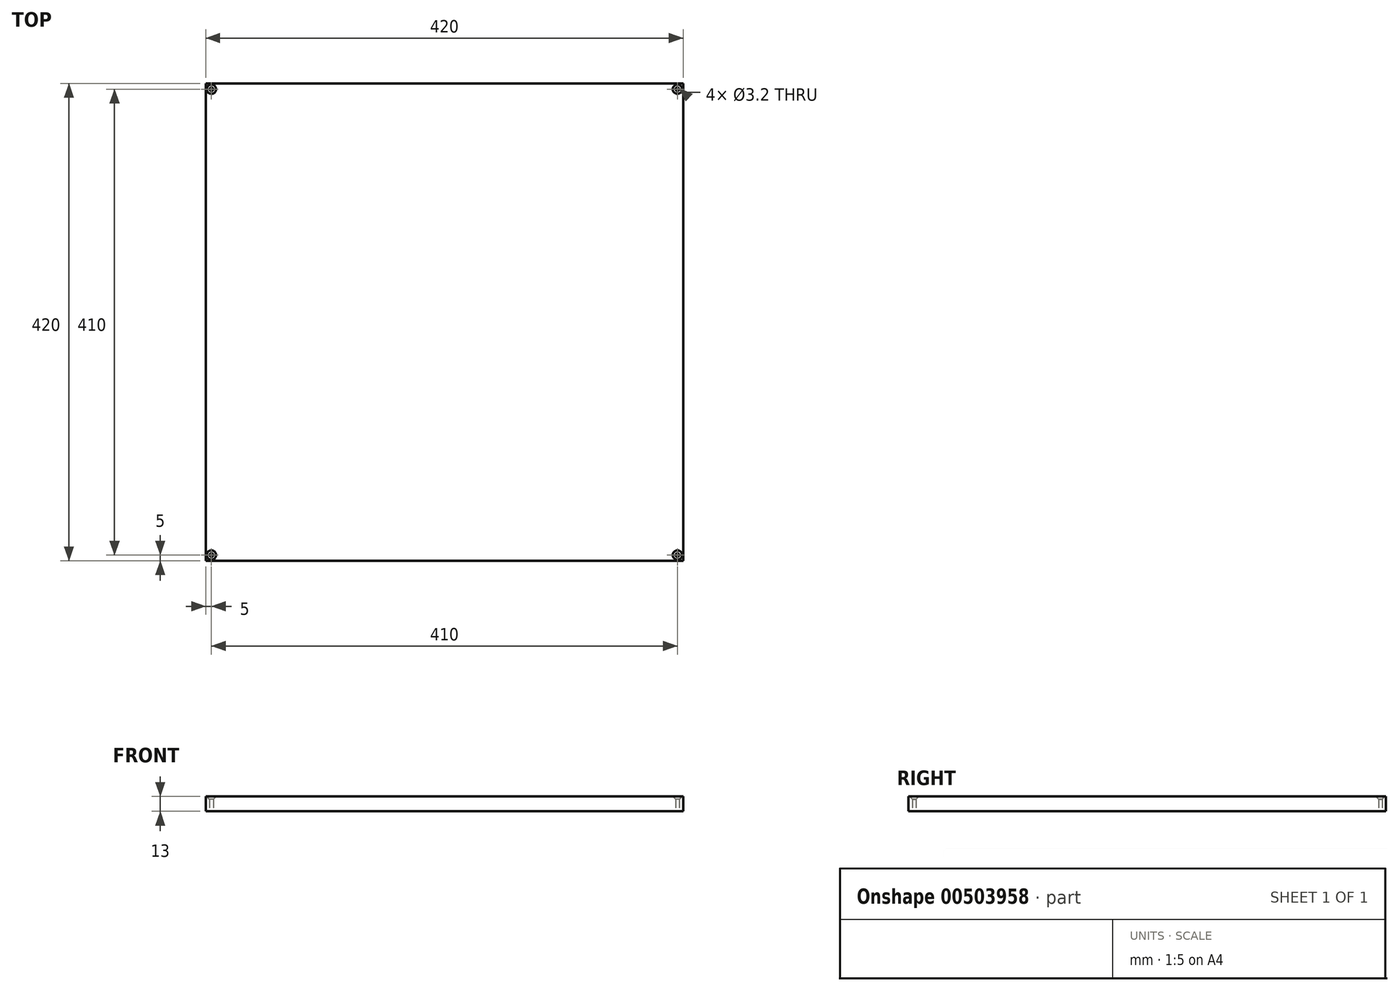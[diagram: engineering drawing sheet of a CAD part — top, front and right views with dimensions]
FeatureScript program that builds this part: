
annotation { "Feature Type Name" : "Feature", "Feature Type Description" : "" }
export const myFeature = defineFeature(function(context is Context, id is Id, definition is map)
    precondition{}
    {
        {
            var Q0;
            Q0=qCreatedBy(makeId("Top.planeOp"),FACE);
            var sketch = newSketch(context, id + "F0", { "sketchPlane" : qUnion([Q0])});
            skLineSegment(sketch, "E0.bottom", {"start": v(210, -210) * mm, "end": v(-210, -210) * mm});
            skLineSegment(sketch, "E0.top", {"start": v(210, 210) * mm, "end": v(-210, 210) * mm});
            skLineSegment(sketch, "E0.left", {"start": v(210, -210) * mm, "end": v(210, 210) * mm});
            skLineSegment(sketch, "E0.right", {"start": v(-210, -210) * mm, "end": v(-210, 210) * mm});
            skPoint(sketch, "E0.middle", {"position": v(0, 0) * mm});
            skLineSegment(sketch, "E1.bottom", {"start": v(205, -205) * mm, "end": v(-205, -205) * mm, "construction": true});
            skLineSegment(sketch, "E1.top", {"start": v(205, 205) * mm, "end": v(-205, 205) * mm, "construction": true});
            skLineSegment(sketch, "E1.left", {"start": v(205, -205) * mm, "end": v(205, 205) * mm, "construction": true});
            skLineSegment(sketch, "E1.right", {"start": v(-205, -205) * mm, "end": v(-205, 205) * mm, "construction": true});
            skCircle(sketch, "E2", {"center": v(-205, 205) * mm, "radius": 1.6 * mm});
            skCircle(sketch, "E3", {"center": v(-205, -205) * mm, "radius": 1.6 * mm});
            skCircle(sketch, "E4", {"center": v(205, -205) * mm, "radius": 1.6 * mm});
            skCircle(sketch, "E5", {"center": v(205, 205) * mm, "radius": 1.6 * mm});
            skSolve(sketch);
        }
        {
            var Q0;
            Q0 = qSketchRegion(id + "F0", true);
            extrude(context, id + "F1", {"entities" : qUnion([Q0]), "depth" : 13 * mm, "offsetDistance" : 25 * mm});
        }
        {
            var Q0;
            Q0=makeQuery(id+"F1.opExtrude","CAP_EDGE",EDGE,{"disambiguationData":[OSD([sQuery(id+"F0.wireOp",EDGE,"E5")])],"isStart":false});
            var Q1;
            Q1=makeQuery(id+"F1.opExtrude","CAP_EDGE",EDGE,{"disambiguationData":[OSD([sQuery(id+"F0.wireOp",EDGE,"E4")])],"isStart":false});
            var Q2;
            Q2=makeQuery(id+"F1.opExtrude","CAP_EDGE",EDGE,{"disambiguationData":[OSD([sQuery(id+"F0.wireOp",EDGE,"E3")])],"isStart":false});
            var Q3;
            Q3=makeQuery(id+"F1.opExtrude","CAP_EDGE",EDGE,{"disambiguationData":[OSD([sQuery(id+"F0.wireOp",EDGE,"E2")])],"isStart":false});
            chamfer(context, id + "F2", {"entities" : qUnion([Q0, Q1, Q2, Q3]), "width" : 2.5 * mm, "tangentPropagation" : true});
        }
    });
